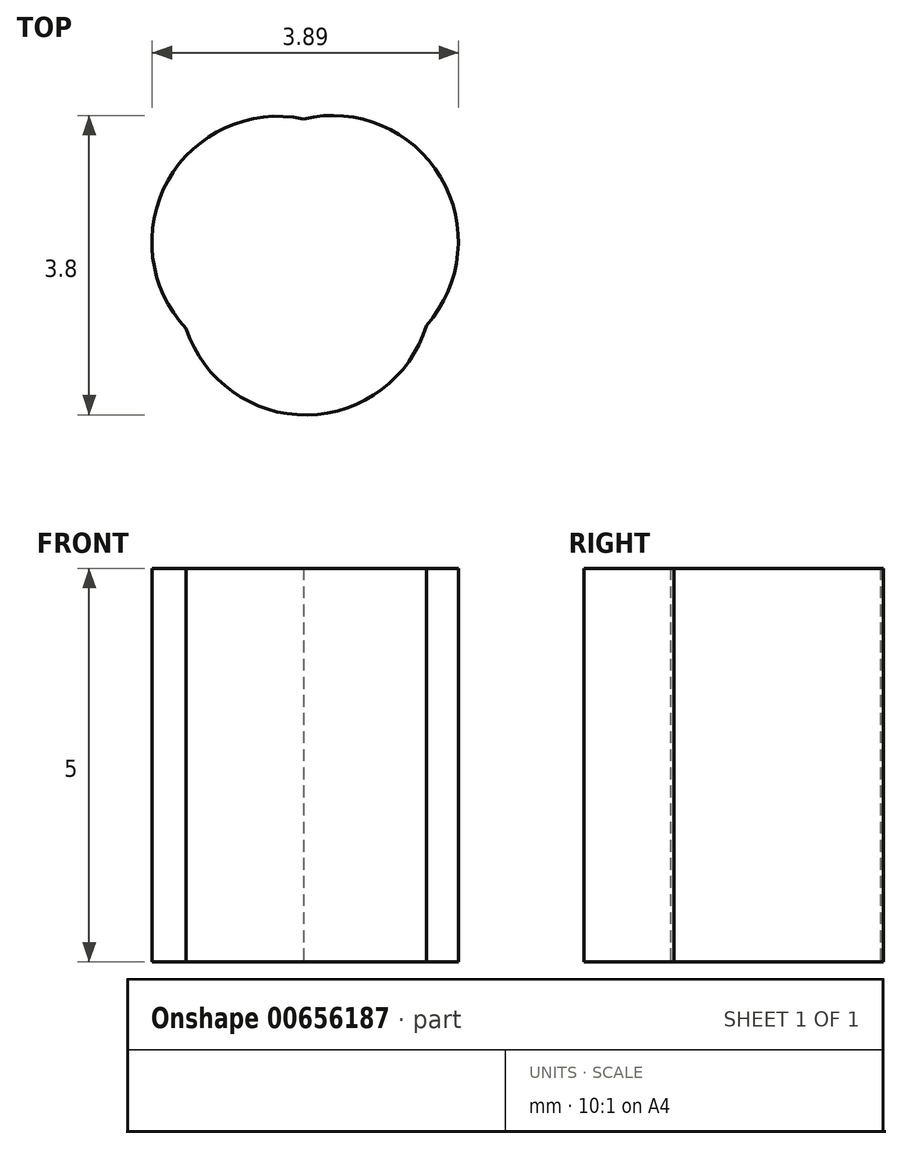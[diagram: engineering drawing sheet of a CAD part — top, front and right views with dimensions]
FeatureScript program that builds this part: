
annotation { "Feature Type Name" : "Feature", "Feature Type Description" : "" }
export const myFeature = defineFeature(function(context is Context, id is Id, definition is map)
    precondition{}
    {
        {
            var Q0;
            Q0=qCreatedBy(makeId("Top.planeOp"),FACE);
            var sketch = newSketch(context, id + "F0", { "sketchPlane" : qUnion([Q0])});
            skCircle(sketch, "E0", {"center": v(-0.35, 0.24) * mm, "radius": 1.6 * mm});
            skCircle(sketch, "E1", {"center": v(0, -0.35) * mm, "radius": 1.6 * mm});
            skCircle(sketch, "E2", {"center": v(0.34, 0.25) * mm, "radius": 1.6 * mm});
            skSolve(sketch);
        }
        {
            var Q0;
            Q0 = qSketchRegion(id + "F0", true);
            var Q1;
            {var subQ0=sQuery(id+"F0.wireOp",EDGE,"E1");var subQ1=sQuery(id+"F0.wireOp",EDGE,"E0");var subQ2=makeQuery(id+"F0.imprint","INTERSECT",VERTEX,{"disambiguationData":[OD(1.0)],"derivedFrom":[subQ1,subQ0]});Q1=makeQuery(id+"F0.imprint","IMPRINT",FACE,{"disambiguationData":[TD([[makeQuery(id+"F0.imprint","IMPRINT",EDGE,{"disambiguationData":[TD([[subQ2,1.0]])],"derivedFrom":subQ1}),1.0]])]});}
            extrude(context, id + "F1", {"entities" : qUnion([Q0, Q1]), "depth" : 5 * mm, "offsetDistance" : 25 * mm});
        }
    });
